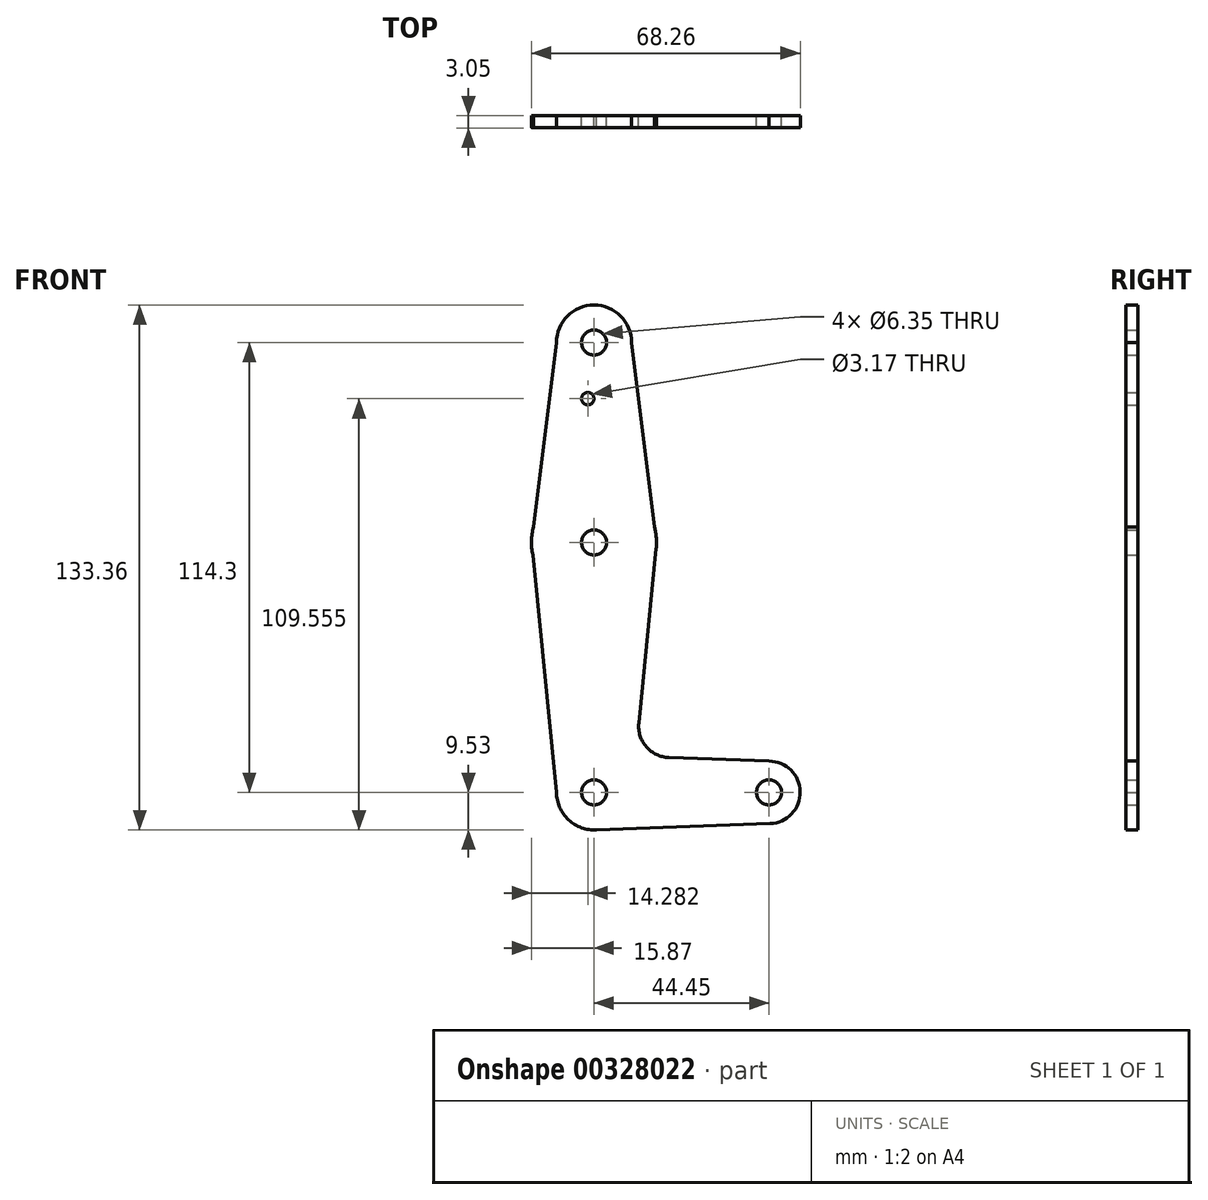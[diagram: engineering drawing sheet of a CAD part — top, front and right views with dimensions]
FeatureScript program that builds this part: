
annotation { "Feature Type Name" : "Feature", "Feature Type Description" : "" }
export const myFeature = defineFeature(function(context is Context, id is Id, definition is map)
    precondition{}
    {
        {
            var Q0;
            Q0=qCreatedBy(makeId("Front.planeOp"),FACE);
            var sketch = newSketch(context, id + "F0", { "sketchPlane" : qUnion([Q0])});
            skLineSegment(sketch, "E0", {"start": v(0, 0) * mm, "end": v(0, 114.3) * mm, "construction": true});
            skLineSegment(sketch, "E1", {"start": v(0, 0) * mm, "end": v(44.45, 0) * mm, "construction": true});
            skCircle(sketch, "E2", {"center": v(0, 114.3) * mm, "radius": 9.53 * mm});
            skCircle(sketch, "E3", {"center": v(0, 63.5) * mm, "radius": 15.88 * mm});
            skCircle(sketch, "E4", {"center": v(0, 0) * mm, "radius": 9.53 * mm});
            skCircle(sketch, "E5", {"center": v(44.45, 0) * mm, "radius": 7.94 * mm});
            skLineSegment(sketch, "E6", {"start": v(0, -9.53) * mm, "end": v(44.73, -7.93) * mm});
            skLineSegment(sketch, "E7", {"start": v(15.39, 67.4) * mm, "end": v(15.88, 63.5) * mm});
            skLineSegment(sketch, "E8", {"start": v(-15.39, 67.4) * mm, "end": v(-15.88, 63.5) * mm});
            skLineSegment(sketch, "E9", {"start": v(-15.88, 63.5) * mm, "end": v(-15.56, 60.36) * mm});
            skLineSegment(sketch, "E10", {"start": v(15.88, 63.5) * mm, "end": v(15.8, 61.92) * mm});
            skLineSegment(sketch, "E11", {"start": v(18.99, 8.85) * mm, "end": v(44.45, 7.94) * mm});
            skCircle(sketch, "E12", {"center": v(0, 114.3) * mm, "radius": 3.18 * mm});
            skCircle(sketch, "E13", {"center": v(0, 63.5) * mm, "radius": 3.18 * mm});
            skCircle(sketch, "E14", {"center": v(0, 0) * mm, "radius": 3.18 * mm});
            skCircle(sketch, "E15", {"center": v(44.45, 0) * mm, "radius": 3.18 * mm});
            skPoint(sketch, "E16.orphan", {"position": v(-9.53, 114.3) * mm});
            skPoint(sketch, "E17.orphan", {"position": v(9.53, 114.3) * mm});
            skPoint(sketch, "E18.orphan", {"position": v(-9.52, 0) * mm});
            skLineSegment(sketch, "E19", {"start": v(-9.53, 114.3) * mm, "end": v(-15.39, 67.4) * mm});
            skLineSegment(sketch, "E20", {"start": v(9.53, 114.3) * mm, "end": v(15.39, 67.4) * mm});
            skLineSegment(sketch, "E21", {"start": v(-15.56, 60.36) * mm, "end": v(-9.52, 0) * mm});
            skLineSegment(sketch, "E22", {"start": v(15.8, 61.92) * mm, "end": v(11.36, 17.58) * mm});
            skCircle(sketch, "E23", {"center": v(-1.59, 100.03) * mm, "radius": 1.59 * mm});
            skArc(sketch, "E24.filletArc", {"start": v(11.36, 17.58) * mm, "mid": v(13.28, 11.56) * mm, "end": v(18.99, 8.85) * mm});
            skSolve(sketch);
        }
        {
            var Q0;
            Q0 = qSketchRegion(id + "F0", true);
            extrude(context, id + "F1", {"entities" : qUnion([Q0]), "depth" : 3.05 * mm});
        }
    });
